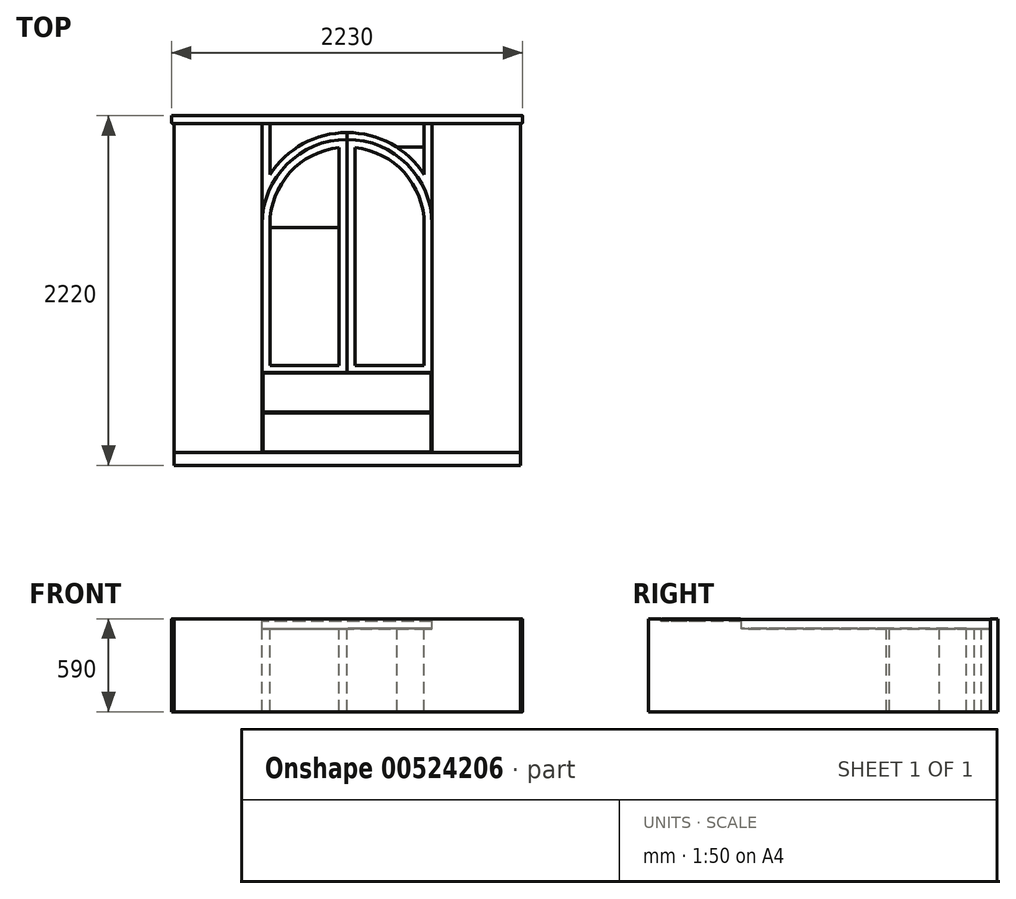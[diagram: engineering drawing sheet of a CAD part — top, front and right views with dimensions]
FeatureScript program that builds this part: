
annotation { "Feature Type Name" : "Feature", "Feature Type Description" : "" }
export const myFeature = defineFeature(function(context is Context, id is Id, definition is map)
    precondition{}
    {
        {
            var Q0;
            Q0=qCreatedBy(makeId("Top.planeOp"),FACE);
            var sketch = newSketch(context, id + "F0", { "sketchPlane" : qUnion([Q0])});
            skLineSegment(sketch, "E0.bottom", {"start": v(0, 0) * mm, "end": v(-2200, 0) * mm});
            skLineSegment(sketch, "E0.top", {"start": v(0, 2220) * mm, "end": v(-2200, 2220) * mm});
            skLineSegment(sketch, "E0.left", {"start": v(0, 0) * mm, "end": v(0, 2170) * mm});
            skLineSegment(sketch, "E0.right", {"start": v(-2200, 0) * mm, "end": v(-2200, 2170) * mm});
            skLineSegment(sketch, "E1", {"start": v(-1100, 2724.28) * mm, "end": v(-1100, 590) * mm, "construction": true});
            skPoint(sketch, "E1.startSnap0", {"position": v(-1100, 2220) * mm});
            skPoint(sketch, "E1.endSnap0", {"position": v(-1100, 0) * mm});
            skLineSegment(sketch, "E2.bottom", {"start": v(-2200, 2220) * mm, "end": v(0, 2220) * mm});
            skLineSegment(sketch, "E2.top", {"start": v(-2200, 2170) * mm, "end": v(-1640, 2170) * mm});
            skLineSegment(sketch, "E3.bottom", {"start": v(-2200, 0) * mm, "end": v(0, 0) * mm});
            skLineSegment(sketch, "E3.top", {"start": v(-2200, 80) * mm, "end": v(0, 80) * mm});
            skLineSegment(sketch, "E3.left", {"start": v(-2200, 0) * mm, "end": v(-2200, 80) * mm});
            skLineSegment(sketch, "E3.right", {"start": v(0, 0) * mm, "end": v(0, 80) * mm});
            skLineSegment(sketch, "E4.bottom", {"start": v(0, 2170) * mm, "end": v(-560, 2170) * mm});
            skLineSegment(sketch, "E4.top", {"start": v(0, 1135) * mm, "end": v(-560, 1135) * mm});
            skLineSegment(sketch, "E4.left", {"start": v(0, 2170) * mm, "end": v(0, 1135) * mm});
            skLineSegment(sketch, "E4.right", {"start": v(-560, 2170) * mm, "end": v(-560, 1135) * mm});
            skLineSegment(sketch, "E5.top", {"start": v(0, 80) * mm, "end": v(-560, 80) * mm});
            skLineSegment(sketch, "E5.left", {"start": v(0, 1135) * mm, "end": v(0, 80) * mm});
            skLineSegment(sketch, "E5.right", {"start": v(-560, 1135) * mm, "end": v(-560, 80) * mm});
            skLineSegment(sketch, "E6.bottom", {"start": v(-560, 80) * mm, "end": v(-1100, 80) * mm});
            skLineSegment(sketch, "E6.top", {"start": v(-560, 590) * mm, "end": v(-1100, 590) * mm});
            skLineSegment(sketch, "E6.left", {"start": v(-560, 80) * mm, "end": v(-560, 590) * mm});
            skLineSegment(sketch, "E7.trimOffspring", {"start": v(-1100, 80) * mm, "end": v(-1100, -610.98) * mm, "construction": true});
            skLineSegment(sketch, "E8.MirrorCS", {"start": v(-1640, 1530) * mm, "end": v(-1640, 1135) * mm});
            skLineSegment(sketch, "E9.MirrorCS", {"start": v(-1640, 1135) * mm, "end": v(-1640, 80) * mm});
            skLineSegment(sketch, "E10.MirrorCS", {"start": v(-2200, 1135) * mm, "end": v(-1640, 1135) * mm});
            skLineSegment(sketch, "E11.MirrorCS", {"start": v(-1640, 590) * mm, "end": v(-1100, 590) * mm});
            skLineSegment(sketch, "E12.bottom", {"start": v(-1635, 585) * mm, "end": v(-565, 585) * mm});
            skLineSegment(sketch, "E12.top", {"start": v(-1635, 337.5) * mm, "end": v(-565, 337.5) * mm});
            skLineSegment(sketch, "E12.left", {"start": v(-1635, 585) * mm, "end": v(-1635, 337.5) * mm});
            skLineSegment(sketch, "E12.right", {"start": v(-565, 585) * mm, "end": v(-565, 337.5) * mm});
            skLineSegment(sketch, "E13.bottom", {"start": v(-565, 332.5) * mm, "end": v(-1635, 332.5) * mm});
            skLineSegment(sketch, "E13.top", {"start": v(-565, 85) * mm, "end": v(-1635, 85) * mm});
            skLineSegment(sketch, "E13.left", {"start": v(-565, 332.5) * mm, "end": v(-565, 85) * mm});
            skLineSegment(sketch, "E13.right", {"start": v(-1635, 332.5) * mm, "end": v(-1635, 85) * mm});
            skLineSegment(sketch, "E14", {"start": v(-1320.22, 2070) * mm, "end": v(-792.57, 2070) * mm, "construction": true});
            skLineSegment(sketch, "E15", {"start": v(-1355.88, 1870) * mm, "end": v(-764.4, 1870) * mm, "construction": true});
            skLineSegment(sketch, "E16.top", {"start": v(-1590, 1511.63) * mm, "end": v(-610, 1511.63) * mm});
            skLineSegment(sketch, "E17", {"start": v(-1801.8, 1530) * mm, "end": v(-139.13, 1530) * mm, "construction": true});
            skArc(sketch, "E18", {"start": v(-1590, 1530) * mm, "mid": v(-1463.73, 1858.33) * mm, "end": v(-1150, 2017.44) * mm});
            skArc(sketch, "E19.MirrorCS", {"start": v(-610, 1530) * mm, "mid": v(-736.27, 1858.33) * mm, "end": v(-1050, 2017.44) * mm});
            skArc(sketch, "E20", {"start": v(-1640, 1530) * mm, "mid": v(-1481.84, 1911.84) * mm, "end": v(-1100, 2070) * mm});
            skArc(sketch, "E21.MirrorCS", {"start": v(-560, 1530) * mm, "mid": v(-718.16, 1911.84) * mm, "end": v(-1100, 2070) * mm});
            skArc(sketch, "E22", {"start": v(-1100, 2113.18) * mm, "mid": v(-821, 2042.1) * mm, "end": v(-610, 1846.22) * mm});
            skArc(sketch, "E23.MirrorCS", {"start": v(-1100, 2113.18) * mm, "mid": v(-1379, 2042.1) * mm, "end": v(-1590, 1846.22) * mm});
            skLineSegment(sketch, "E24.bottom", {"start": v(-1640, 2170) * mm, "end": v(-1100, 2170) * mm});
            skLineSegment(sketch, "E24.left", {"start": v(-1640, 2170) * mm, "end": v(-1640, 590) * mm});
            skLineSegment(sketch, "E24.right", {"start": v(-1100, 2170) * mm, "end": v(-1100, 590) * mm});
            skLineSegment(sketch, "E25.trimOffspring", {"start": v(-1100, 2170) * mm, "end": v(0, 2170) * mm});
            skLineSegment(sketch, "E26.top", {"start": v(-1590, 635) * mm, "end": v(-1150, 635) * mm});
            skLineSegment(sketch, "E26.left", {"start": v(-1590, 1530) * mm, "end": v(-1590, 635) * mm});
            skLineSegment(sketch, "E26.right", {"start": v(-1150, 1530) * mm, "end": v(-1150, 635) * mm});
            skLineSegment(sketch, "E27", {"start": v(-1150, 1530) * mm, "end": v(-1150, 2017.44) * mm});
            skPoint(sketch, "E28.orphan", {"position": v(-1100, 2020) * mm});
            skLineSegment(sketch, "E29.trimOffspring", {"start": v(-1590, 1530) * mm, "end": v(-1590, 1511.63) * mm});
            skLineSegment(sketch, "E30.trimOffspring", {"start": v(-1590, 1846.22) * mm, "end": v(-1590, 2170) * mm});
            skLineSegment(sketch, "E31", {"start": v(-610, 1846.22) * mm, "end": v(-610, 2170) * mm});
            skLineSegment(sketch, "E32.MirrorCS", {"start": v(-610, 1530) * mm, "end": v(-610, 635) * mm});
            skLineSegment(sketch, "E33.MirrorCS", {"start": v(-610, 635) * mm, "end": v(-1050, 635) * mm});
            skLineSegment(sketch, "E34.MirrorCS", {"start": v(-1050, 1530) * mm, "end": v(-1050, 635) * mm});
            skLineSegment(sketch, "E35.MirrorCS", {"start": v(-1050, 1530) * mm, "end": v(-1050, 2017.44) * mm});
            skLineSegment(sketch, "E36.trimOffspring", {"start": v(-1100, 2020) * mm, "end": v(-610, 2020) * mm});
            skLineSegment(sketch, "E37.bottom", {"start": v(0, 2220) * mm, "end": v(15, 2220) * mm});
            skLineSegment(sketch, "E37.top", {"start": v(0, 2170) * mm, "end": v(15, 2170) * mm});
            skLineSegment(sketch, "E37.right", {"start": v(15, 2220) * mm, "end": v(15, 2170) * mm});
            skLineSegment(sketch, "E38.bottom", {"start": v(-2200, 2220) * mm, "end": v(-2215, 2220) * mm});
            skLineSegment(sketch, "E38.top", {"start": v(-2200, 2170) * mm, "end": v(-2215, 2170) * mm});
            skLineSegment(sketch, "E38.right", {"start": v(-2215, 2220) * mm, "end": v(-2215, 2170) * mm});
            skSolve(sketch);
        }
        {
            var Q0;
            {var subQ4=sQuery(id+"F0.wireOp",EDGE,"E10.MirrorCS");var subQ10=makeQuery(id+"F0.imprint","IMPRINT",EDGE,{"derivedFrom":subQ4});var subQ13=sQuery(id+"F0.wireOp",EDGE,"E4.bottom");var subQ16=sQuery(id+"F0.wireOp",EDGE,"E4.top");var subQ17=makeQuery(id+"F0.imprint","IMPRINT",EDGE,{"derivedFrom":subQ16});var subQ21=makeQuery(id+"F0.imprint","IMPRINT",EDGE,{"derivedFrom":subQ13});var subQ24=sQuery(id+"F0.wireOp",EDGE,"E0.bottom");var subQ34=sQuery(id+"F0.wireOp",EDGE,"E2.top");var subQ37=makeQuery(id+"F0.imprint","IMPRINT",EDGE,{"derivedFrom":subQ34});Q0=qUnion([makeQuery(id+"F0.imprint","IMPRINT",FACE,{"disambiguationData":[TD([[subQ37,-1.0]])]}),makeQuery(id+"F0.imprint","IMPRINT",FACE,{"disambiguationData":[TD([[makeQuery(id+"F0.imprint","IMPRINT",EDGE,{"derivedFrom":sQuery(id+"F0.wireOp",EDGE,"E0.top")}),1.0]])]}),makeQuery(id+"F0.imprint","IMPRINT",FACE,{"disambiguationData":[TD([[subQ17,1.0]])]}),makeQuery(id+"F0.imprint","IMPRINT",FACE,{"disambiguationData":[TD([[makeQuery(id+"F0.imprint","IMPRINT",EDGE,{"derivedFrom":subQ24}),-1.0]])]}),makeQuery(id+"F0.imprint","IMPRINT",FACE,{"disambiguationData":[TD([[subQ21,1.0]])]}),makeQuery(id+"F0.imprint","IMPRINT",FACE,{"disambiguationData":[TD([[subQ10,-1.0]])]})]);}
            var Q1;
            Q1=makeQuery(id+"F0.imprint","IMPRINT",FACE,{"disambiguationData":[TD([[makeQuery(id+"F0.imprint","IMPRINT",EDGE,{"derivedFrom":sQuery(id+"F0.wireOp",EDGE,"E12.bottom")}),-1.0]])]});
            var Q2;
            Q2=makeQuery(id+"F0.imprint","IMPRINT",FACE,{"disambiguationData":[TD([[makeQuery(id+"F0.imprint","IMPRINT",EDGE,{"derivedFrom":sQuery(id+"F0.wireOp",EDGE,"E13.bottom")}),1.0]])]});
            var Q3;
            {var subQ5=sQuery(id+"F0.wireOp",EDGE,"E33.MirrorCS");Q3=makeQuery(id+"F0.imprint","IMPRINT",FACE,{"disambiguationData":[TD([[makeQuery(id+"F0.imprint","IMPRINT",EDGE,{"derivedFrom":subQ5}),-1.0]])]});}
            var Q4;
            {var subQ5=sQuery(id+"F0.wireOp",EDGE,"E26.top");Q4=makeQuery(id+"F0.imprint","IMPRINT",FACE,{"disambiguationData":[TD([[makeQuery(id+"F0.imprint","IMPRINT",EDGE,{"derivedFrom":subQ5}),1.0]])]});}
            var Q5;
            {var subQ4=sQuery(id+"F0.wireOp",EDGE,"E18");Q5=makeQuery(id+"F0.imprint","IMPRINT",FACE,{"disambiguationData":[TD([[makeQuery(id+"F0.imprint","IMPRINT",EDGE,{"derivedFrom":subQ4}),-1.0]])]});}
            var Q6;
            {var subQ1=sQuery(id+"F0.wireOp",EDGE,"E19.MirrorCS");Q6=makeQuery(id+"F0.imprint","IMPRINT",FACE,{"disambiguationData":[TD([[makeQuery(id+"F0.imprint","IMPRINT",EDGE,{"derivedFrom":subQ1}),1.0]])]});}
            var Q7;
            {var subQ0=sQuery(id+"F0.wireOp",EDGE,"E23.MirrorCS");Q7=makeQuery(id+"F0.imprint","IMPRINT",FACE,{"disambiguationData":[TD([[makeQuery(id+"F0.imprint","IMPRINT",EDGE,{"derivedFrom":subQ0}),-1.0]])]});}
            var Q8;
            {var subQ0=sQuery(id+"F0.wireOp",EDGE,"E31");var subQ1=sQuery(id+"F0.wireOp",EDGE,"E25.trimOffspring");var subQ2=makeQuery(id+"F0.imprint","INTERSECT",VERTEX,{"derivedFrom":[subQ1,subQ0]});Q8=makeQuery(id+"F0.imprint","IMPRINT",FACE,{"disambiguationData":[TD([[makeQuery(id+"F0.imprint","IMPRINT",EDGE,{"disambiguationData":[TD([[subQ2,1.0]])],"derivedFrom":subQ0}),1.0]])]});}
            var Q9;
            {var subQ0=sQuery(id+"F0.wireOp",EDGE,"E31");var subQ1=sQuery(id+"F0.wireOp",EDGE,"E22");var subQ2=makeQuery(id+"F0.imprint","INTERSECT",VERTEX,{"derivedFrom":[subQ1,subQ0]});Q9=makeQuery(id+"F0.imprint","IMPRINT",FACE,{"disambiguationData":[TD([[makeQuery(id+"F0.imprint","IMPRINT",EDGE,{"disambiguationData":[TD([[subQ2,1.0]])],"derivedFrom":subQ1}),1.0]])]});}
            var Q10;
            {var subQ4=sQuery(id+"F0.wireOp",EDGE,"E20");Q10=makeQuery(id+"F0.imprint","IMPRINT",FACE,{"disambiguationData":[TD([[makeQuery(id+"F0.imprint","IMPRINT",EDGE,{"derivedFrom":subQ4}),1.0]])]});}
            var Q11;
            {var subQ6=sQuery(id+"F0.wireOp",EDGE,"E8.MirrorCS");Q11=makeQuery(id+"F0.imprint","IMPRINT",FACE,{"disambiguationData":[TD([[makeQuery(id+"F0.imprint","IMPRINT",EDGE,{"derivedFrom":subQ6}),1.0]])]});}
            var Q12;
            {var subQ10=sQuery(id+"F0.wireOp",EDGE,"E6.top");Q12=makeQuery(id+"F0.imprint","IMPRINT",FACE,{"disambiguationData":[TD([[makeQuery(id+"F0.imprint","IMPRINT",EDGE,{"derivedFrom":subQ10}),-1.0]])]});}
            var Q13;
            {var subQ1=sQuery(id+"F0.wireOp",EDGE,"E4.right");var subQ9=sQuery(id+"F0.wireOp",EDGE,"E21.MirrorCS");var subQ10=makeQuery(id+"F0.imprint","INTERSECT",VERTEX,{"derivedFrom":[subQ1,subQ9]});Q13=makeQuery(id+"F0.imprint","IMPRINT",FACE,{"disambiguationData":[TD([[makeQuery(id+"F0.imprint","IMPRINT",EDGE,{"disambiguationData":[TD([[subQ10,-1.0]])],"derivedFrom":subQ9}),-1.0]])]});}
            var Q14;
            {var subQ3=sQuery(id+"F0.wireOp",EDGE,"E36.trimOffspring");var subQ5=sQuery(id+"F0.wireOp",EDGE,"E22");var subQ7=makeQuery(id+"F0.imprint","INTERSECT",VERTEX,{"derivedFrom":[subQ5,subQ3]});Q14=makeQuery(id+"F0.imprint","IMPRINT",FACE,{"disambiguationData":[TD([[makeQuery(id+"F0.imprint","IMPRINT",EDGE,{"disambiguationData":[TD([[subQ7,1.0]])],"derivedFrom":subQ3}),1.0]])]});}
            var Q15;
            {var subQ0=sQuery(id+"F0.wireOp",EDGE,"E24.right");var subQ3=sQuery(id+"F0.wireOp",EDGE,"E36.trimOffspring");var subQ5=makeQuery(id+"F0.imprint","INTERSECT",VERTEX,{"derivedFrom":[subQ0,subQ3]});Q15=makeQuery(id+"F0.imprint","IMPRINT",FACE,{"disambiguationData":[TD([[makeQuery(id+"F0.imprint","IMPRINT",EDGE,{"disambiguationData":[TD([[subQ5,-1.0]])],"derivedFrom":subQ3}),1.0]])]});}
            var Q16;
            {var subQ7=sQuery(id+"F0.wireOp",EDGE,"E6.top");Q16=makeQuery(id+"F0.imprint","IMPRINT",FACE,{"disambiguationData":[TD([[makeQuery(id+"F0.imprint","IMPRINT",EDGE,{"derivedFrom":subQ7}),1.0]])]});}
            extrude(context, id + "F1", {"entities" : qUnion([Q0, Q1, Q2, Q3, Q4, Q5, Q6, Q7, Q8, Q9, Q10, Q11, Q12, Q13, Q14, Q15, Q16]), "oppositeDirection" : true, "depth" : 590 * mm, "offsetDistance" : 25 * mm});
        }
        {
            var Q0;
            Q0=makeQuery(id+"F1.opExtrude","SWEPT_EDGE",EDGE,{"disambiguationData":[OSD([sQuery(id+"F0.wireOp",EDGE,"E37.top"),sQuery(id+"F0.wireOp",EDGE,"E37.right")])]});
            var Q1;
            Q1=makeQuery(id+"F1.opExtrude","SWEPT_EDGE",EDGE,{"disambiguationData":[OSD([sQuery(id+"F0.wireOp",EDGE,"E38.top"),sQuery(id+"F0.wireOp",EDGE,"E38.right")])]});
            fillet(context, id + "F2", {"entities" : qUnion([Q0, Q1]), "radius" : 10 * mm, "tangentPropagation" : true, "allowEdgeOverflow" : false});
        }
        {
            var Q0;
            {var subQ0=sQuery(id+"F0.wireOp",EDGE,"E23.MirrorCS");Q0=makeQuery(id+"F0.imprint","IMPRINT",FACE,{"disambiguationData":[TD([[makeQuery(id+"F0.imprint","IMPRINT",EDGE,{"derivedFrom":subQ0}),-1.0]])]});}
            var Q1;
            {var subQ0=sQuery(id+"F0.wireOp",EDGE,"E31");var subQ1=sQuery(id+"F0.wireOp",EDGE,"E25.trimOffspring");var subQ2=makeQuery(id+"F0.imprint","INTERSECT",VERTEX,{"derivedFrom":[subQ1,subQ0]});Q1=makeQuery(id+"F0.imprint","IMPRINT",FACE,{"disambiguationData":[TD([[makeQuery(id+"F0.imprint","IMPRINT",EDGE,{"disambiguationData":[TD([[subQ2,1.0]])],"derivedFrom":subQ0}),1.0]])]});}
            var Q2;
            {var subQ0=sQuery(id+"F0.wireOp",EDGE,"E31");var subQ1=sQuery(id+"F0.wireOp",EDGE,"E22");var subQ2=makeQuery(id+"F0.imprint","INTERSECT",VERTEX,{"derivedFrom":[subQ1,subQ0]});Q2=makeQuery(id+"F0.imprint","IMPRINT",FACE,{"disambiguationData":[TD([[makeQuery(id+"F0.imprint","IMPRINT",EDGE,{"disambiguationData":[TD([[subQ2,1.0]])],"derivedFrom":subQ1}),1.0]])]});}
            extrude(context, id + "F3", {"entities" : qUnion([Q0, Q1, Q2]), "operationType" : NewBodyOperationType.REMOVE, "oppositeDirection" : true, "depth" : 65 * mm, "offsetDistance" : 25 * mm});
        }
        {
            var Q0;
            {var subQ4=sQuery(id+"F0.wireOp",EDGE,"E20");Q0=makeQuery(id+"F0.imprint","IMPRINT",FACE,{"disambiguationData":[TD([[makeQuery(id+"F0.imprint","IMPRINT",EDGE,{"derivedFrom":subQ4}),1.0]])]});}
            var Q1;
            {var subQ3=sQuery(id+"F0.wireOp",EDGE,"E36.trimOffspring");var subQ5=sQuery(id+"F0.wireOp",EDGE,"E22");var subQ7=makeQuery(id+"F0.imprint","INTERSECT",VERTEX,{"derivedFrom":[subQ5,subQ3]});Q1=makeQuery(id+"F0.imprint","IMPRINT",FACE,{"disambiguationData":[TD([[makeQuery(id+"F0.imprint","IMPRINT",EDGE,{"disambiguationData":[TD([[subQ7,1.0]])],"derivedFrom":subQ3}),1.0]])]});}
            var Q2;
            {var subQ1=sQuery(id+"F0.wireOp",EDGE,"E4.right");var subQ9=sQuery(id+"F0.wireOp",EDGE,"E21.MirrorCS");var subQ10=makeQuery(id+"F0.imprint","INTERSECT",VERTEX,{"derivedFrom":[subQ1,subQ9]});Q2=makeQuery(id+"F0.imprint","IMPRINT",FACE,{"disambiguationData":[TD([[makeQuery(id+"F0.imprint","IMPRINT",EDGE,{"disambiguationData":[TD([[subQ10,-1.0]])],"derivedFrom":subQ9}),-1.0]])]});}
            extrude(context, id + "F4", {"entities" : qUnion([Q0, Q1, Q2]), "operationType" : NewBodyOperationType.REMOVE, "oppositeDirection" : true, "depth" : 64 * mm, "offsetDistance" : 25 * mm});
        }
        {
            var Q0;
            {var subQ6=sQuery(id+"F0.wireOp",EDGE,"E8.MirrorCS");Q0=makeQuery(id+"F0.imprint","IMPRINT",FACE,{"disambiguationData":[TD([[makeQuery(id+"F0.imprint","IMPRINT",EDGE,{"derivedFrom":subQ6}),1.0]])]});}
            var Q1;
            {var subQ0=sQuery(id+"F0.wireOp",EDGE,"E24.right");var subQ3=sQuery(id+"F0.wireOp",EDGE,"E36.trimOffspring");var subQ5=makeQuery(id+"F0.imprint","INTERSECT",VERTEX,{"derivedFrom":[subQ0,subQ3]});Q1=makeQuery(id+"F0.imprint","IMPRINT",FACE,{"disambiguationData":[TD([[makeQuery(id+"F0.imprint","IMPRINT",EDGE,{"disambiguationData":[TD([[subQ5,-1.0]])],"derivedFrom":subQ3}),1.0]])]});}
            var Q2;
            {var subQ10=sQuery(id+"F0.wireOp",EDGE,"E6.top");Q2=makeQuery(id+"F0.imprint","IMPRINT",FACE,{"disambiguationData":[TD([[makeQuery(id+"F0.imprint","IMPRINT",EDGE,{"derivedFrom":subQ10}),-1.0]])]});}
            extrude(context, id + "F5", {"entities" : qUnion([Q0, Q1, Q2]), "operationType" : NewBodyOperationType.REMOVE, "oppositeDirection" : true, "depth" : 62 * mm, "offsetDistance" : 25 * mm});
        }
        {
            var Q0;
            {var subQ5=sQuery(id+"F0.wireOp",EDGE,"E26.top");Q0=makeQuery(id+"F0.imprint","IMPRINT",FACE,{"disambiguationData":[TD([[makeQuery(id+"F0.imprint","IMPRINT",EDGE,{"derivedFrom":subQ5}),1.0]])]});}
            var Q1;
            {var subQ5=sQuery(id+"F0.wireOp",EDGE,"E33.MirrorCS");Q1=makeQuery(id+"F0.imprint","IMPRINT",FACE,{"disambiguationData":[TD([[makeQuery(id+"F0.imprint","IMPRINT",EDGE,{"derivedFrom":subQ5}),-1.0]])]});}
            var Q2;
            {var subQ1=sQuery(id+"F0.wireOp",EDGE,"E19.MirrorCS");Q2=makeQuery(id+"F0.imprint","IMPRINT",FACE,{"disambiguationData":[TD([[makeQuery(id+"F0.imprint","IMPRINT",EDGE,{"derivedFrom":subQ1}),1.0]])]});}
            var Q3;
            {var subQ4=sQuery(id+"F0.wireOp",EDGE,"E18");Q3=makeQuery(id+"F0.imprint","IMPRINT",FACE,{"disambiguationData":[TD([[makeQuery(id+"F0.imprint","IMPRINT",EDGE,{"derivedFrom":subQ4}),-1.0]])]});}
            extrude(context, id + "F6", {"entities" : qUnion([Q0, Q1, Q2, Q3]), "operationType" : NewBodyOperationType.REMOVE, "oppositeDirection" : true, "depth" : 63 * mm, "offsetDistance" : 25 * mm});
        }
        {
            var Q0;
            {var subQ1=sQuery(id+"F0.wireOp",EDGE,"E2.top");Q0=makeQuery(id+"F0.imprint","IMPRINT",FACE,{"disambiguationData":[TD([[makeQuery(id+"F0.imprint","IMPRINT",EDGE,{"derivedFrom":subQ1}),-1.0]])]});}
            var Q1;
            {var subQ4=sQuery(id+"F0.wireOp",EDGE,"E10.MirrorCS");Q1=makeQuery(id+"F0.imprint","IMPRINT",FACE,{"disambiguationData":[TD([[makeQuery(id+"F0.imprint","IMPRINT",EDGE,{"derivedFrom":subQ4}),-1.0]])]});}
            var Q2;
            {var subQ1=sQuery(id+"F0.wireOp",EDGE,"E4.bottom");Q2=makeQuery(id+"F0.imprint","IMPRINT",FACE,{"disambiguationData":[TD([[makeQuery(id+"F0.imprint","IMPRINT",EDGE,{"derivedFrom":subQ1}),1.0]])]});}
            var Q3;
            {var subQ0=sQuery(id+"F0.wireOp",EDGE,"E4.top");Q3=makeQuery(id+"F0.imprint","IMPRINT",FACE,{"disambiguationData":[TD([[makeQuery(id+"F0.imprint","IMPRINT",EDGE,{"derivedFrom":subQ0}),1.0]])]});}
            extrude(context, id + "F7", {"entities" : qUnion([Q0, Q1, Q2, Q3]), "operationType" : NewBodyOperationType.REMOVE, "oppositeDirection" : true, "depth" : 5 * mm, "offsetDistance" : 25 * mm});
        }
        {
            var Q0;
            {var subQ0=sQuery(id+"F0.wireOp",EDGE,"E25.trimOffspring");var subQ1=sQuery(id+"F0.wireOp",EDGE,"E24.bottom");Q0=makeQuery(id+"F7.boolean.opBoolean","MERGE",EDGE,{"derivedFrom":[makeQuery(id+"F1.opExtrude","CAP_EDGE",EDGE,{"disambiguationData":[OSD([sQuery(id+"F0.wireOp",EDGE,"E37.top")])],"isStart":true}),makeQuery(id+"F1.opExtrude","CAP_EDGE",EDGE,{"disambiguationData":[OSD([sQuery(id+"F0.wireOp",EDGE,"E38.top")])],"isStart":true}),makeQuery(id+"F4.boolean.opBoolean","MERGE",EDGE,{"derivedFrom":[makeQuery(id+"F3.boolean.opBoolean","COPY",EDGE,{"derivedFrom":makeQuery(id+"F3.opExtrude","CAP_EDGE",EDGE,{"disambiguationData":[OSD([subQ1,subQ0])],"isStart":true})})],"fromTools":[makeQuery(id+"F4.opExtrude","CAP_EDGE",EDGE,{"disambiguationData":[OSD([subQ1])],"isStart":true}),makeQuery(id+"F4.opExtrude","CAP_EDGE",EDGE,{"disambiguationData":[OSD([subQ0])],"isStart":true})]})],"fromTools":[makeQuery(id+"F7.opExtrude","CAP_EDGE",EDGE,{"disambiguationData":[OSD([sQuery(id+"F0.wireOp",EDGE,"E2.top")])],"isStart":true}),makeQuery(id+"F7.opExtrude","CAP_EDGE",EDGE,{"disambiguationData":[OSD([sQuery(id+"F0.wireOp",EDGE,"E4.bottom")])],"isStart":true})]});}
            fillet(context, id + "F8", {"entities" : qUnion([Q0]), "radius" : 5 * mm, "tangentPropagation" : true, "allowEdgeOverflow" : false});
        }
        {
            var Q0;
            {var subQ7=sQuery(id+"F0.wireOp",EDGE,"E6.top");Q0=makeQuery(id+"F0.imprint","IMPRINT",FACE,{"disambiguationData":[TD([[makeQuery(id+"F0.imprint","IMPRINT",EDGE,{"derivedFrom":subQ7}),1.0]])]});}
            extrude(context, id + "F9", {"entities" : qUnion([Q0]), "operationType" : NewBodyOperationType.REMOVE, "oppositeDirection" : true, "depth" : 18 * mm, "offsetDistance" : 25 * mm});
        }
        {
            var Q0;
            Q0=makeQuery(id+"F7.boolean.opBoolean","COPY",EDGE,{"derivedFrom":makeQuery(id+"F7.opExtrude","CAP_EDGE",EDGE,{"disambiguationData":[OSD([sQuery(id+"F0.wireOp",EDGE,"E0.right")])],"isStart":false})});
            var Q1;
            {var subQ0=sQuery(id+"F0.wireOp",EDGE,"E24.left");var subQ1=sQuery(id+"F0.wireOp",EDGE,"E9.MirrorCS");var subQ2=sQuery(id+"F0.wireOp",EDGE,"E8.MirrorCS");var subQ4=makeQuery(id+"F7.opExtrude","CAP_EDGE",EDGE,{"disambiguationData":[OSD([subQ2,subQ1,subQ0])],"isStart":false});Q1=makeQuery(id+"F9.boolean.opBoolean","MERGE",EDGE,{"derivedFrom":[makeQuery(id+"F7.boolean.opBoolean","COPY",EDGE,{"disambiguationData":[topologyDisambiguationEdgeConnected([makeQuery(id+"F4.boolean.opBoolean","COPY",FACE,{"derivedFrom":makeQuery(id+"F4.opExtrude","SWEPT_FACE",FACE,{"disambiguationData":[OSD([subQ0])]})})])],"derivedFrom":subQ4}),makeQuery(id+"F7.boolean.opBoolean","COPY",EDGE,{"disambiguationData":[topologyDisambiguationEdgeConnected([makeQuery(id+"F7.opExtrude","SWEPT_FACE",FACE,{"disambiguationData":[OSD([subQ2,subQ1,subQ0])]})])],"derivedFrom":subQ4})]});}
            var Q2;
            Q2=makeQuery(id+"F5.boolean.opBoolean","COPY",EDGE,{"derivedFrom":makeQuery(id+"F5.opExtrude","CAP_EDGE",EDGE,{"disambiguationData":[OSD([sQuery(id+"F0.wireOp",EDGE,"E20"),sQuery(id+"F0.wireOp",EDGE,"E21.MirrorCS")])],"isStart":false})});
            var Q3;
            Q3=makeQuery(id+"F6.boolean.opBoolean","COPY",EDGE,{"derivedFrom":makeQuery(id+"F6.opExtrude","CAP_EDGE",EDGE,{"disambiguationData":[OSD([sQuery(id+"F0.wireOp",EDGE,"E26.right"),sQuery(id+"F0.wireOp",EDGE,"E27")])],"isStart":false})});
            var Q4;
            Q4=makeQuery(id+"F5.boolean.opBoolean","COPY",EDGE,{"derivedFrom":makeQuery(id+"F5.opExtrude","CAP_EDGE",EDGE,{"disambiguationData":[OSD([sQuery(id+"F0.wireOp",EDGE,"E34.MirrorCS"),sQuery(id+"F0.wireOp",EDGE,"E35.MirrorCS")])],"isStart":false})});
            var Q5;
            Q5=makeQuery(id+"F5.boolean.opBoolean","COPY",EDGE,{"derivedFrom":makeQuery(id+"F5.opExtrude","CAP_EDGE",EDGE,{"disambiguationData":[OSD([sQuery(id+"F0.wireOp",EDGE,"E19.MirrorCS")])],"isStart":false})});
            var Q6;
            Q6=makeQuery(id+"F5.boolean.opBoolean","COPY",EDGE,{"derivedFrom":makeQuery(id+"F5.opExtrude","CAP_EDGE",EDGE,{"disambiguationData":[OSD([sQuery(id+"F0.wireOp",EDGE,"E32.MirrorCS")])],"isStart":false})});
            var Q7;
            Q7=makeQuery(id+"F5.boolean.opBoolean","COPY",EDGE,{"derivedFrom":makeQuery(id+"F5.opExtrude","CAP_EDGE",EDGE,{"disambiguationData":[OSD([sQuery(id+"F0.wireOp",EDGE,"E33.MirrorCS")])],"isStart":false})});
            var Q8;
            Q8=makeQuery(id+"F5.boolean.opBoolean","COPY",EDGE,{"derivedFrom":makeQuery(id+"F5.opExtrude","CAP_EDGE",EDGE,{"disambiguationData":[OSD([sQuery(id+"F0.wireOp",EDGE,"E26.top")])],"isStart":false})});
            var Q9;
            Q9=makeQuery(id+"F4.boolean.opBoolean","COPY",EDGE,{"derivedFrom":makeQuery(id+"F4.opExtrude","CAP_EDGE",EDGE,{"disambiguationData":[OSD([sQuery(id+"F0.wireOp",EDGE,"E22"),sQuery(id+"F0.wireOp",EDGE,"E23.MirrorCS")])],"isStart":false})});
            var Q10;
            {var subQ0=sQuery(id+"F0.wireOp",EDGE,"E4.right");var subQ1=sQuery(id+"F0.wireOp",EDGE,"E5.right");var subQ3=makeQuery(id+"F7.opExtrude","CAP_EDGE",EDGE,{"disambiguationData":[OSD([subQ0,subQ1])],"isStart":false});Q10=makeQuery(id+"F9.boolean.opBoolean","MERGE",EDGE,{"derivedFrom":[makeQuery(id+"F7.boolean.opBoolean","COPY",EDGE,{"disambiguationData":[topologyDisambiguationEdgeConnected([makeQuery(id+"F7.opExtrude","SWEPT_FACE",FACE,{"disambiguationData":[OSD([subQ0,subQ1])]})])],"derivedFrom":subQ3}),makeQuery(id+"F7.boolean.opBoolean","COPY",EDGE,{"disambiguationData":[topologyDisambiguationEdgeConnected([makeQuery(id+"F4.boolean.opBoolean","COPY",FACE,{"derivedFrom":makeQuery(id+"F4.opExtrude","SWEPT_FACE",FACE,{"disambiguationData":[OSD([subQ0])]})})])],"derivedFrom":subQ3})]});}
            var Q11;
            Q11=makeQuery(id+"F7.boolean.opBoolean","COPY",EDGE,{"derivedFrom":makeQuery(id+"F7.opExtrude","CAP_EDGE",EDGE,{"disambiguationData":[OSD([sQuery(id+"F0.wireOp",EDGE,"E0.left")])],"isStart":false})});
            fillet(context, id + "F10", {"entities" : qUnion([Q0, Q1, Q2, Q3, Q4, Q5, Q6, Q7, Q8, Q9, Q10, Q11]), "radius" : 5 * mm, "tangentPropagation" : true, "allowEdgeOverflow" : false});
        }
    });
